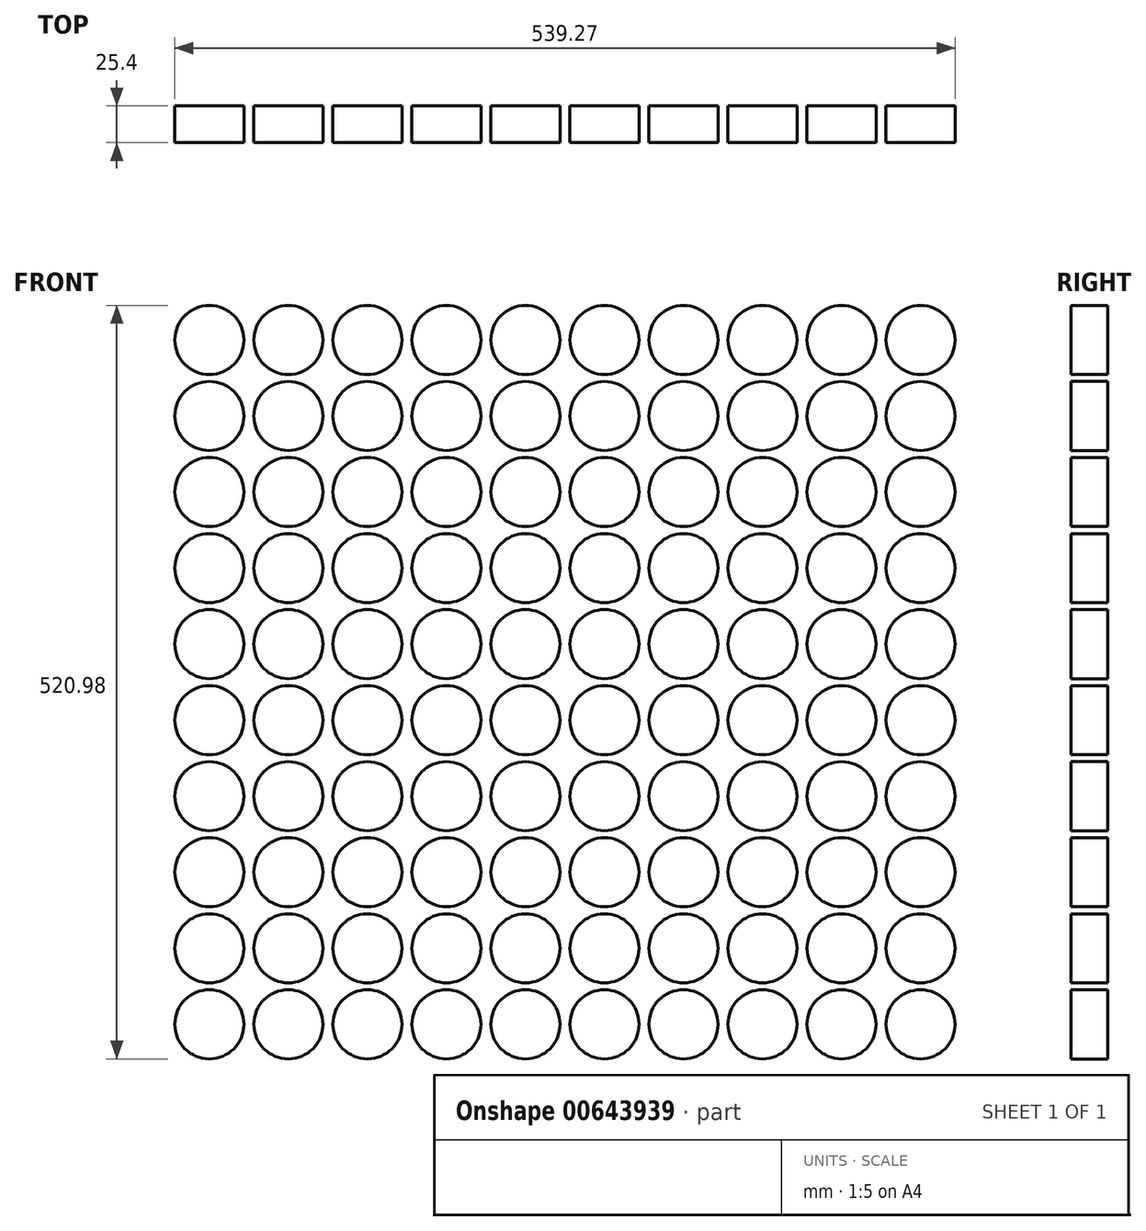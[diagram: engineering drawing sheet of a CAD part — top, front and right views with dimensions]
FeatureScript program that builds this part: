
annotation { "Feature Type Name" : "Feature", "Feature Type Description" : "" }
export const myFeature = defineFeature(function(context is Context, id is Id, definition is map)
    precondition{}
    {
        {
            var Q0;
            Q0=qCreatedBy(makeId("Front.planeOp"),FACE);
            var sketch = newSketch(context, id + "F0", { "sketchPlane" : qUnion([Q0])});
            skCircle(sketch, "E0", {"center": v(-116.75, -34.96) * mm, "radius": 23.89 * mm});
            skCircle(sketch, "E1.0.1.0", {"center": v(-116.75, 17.62) * mm, "radius": 23.89 * mm});
            skCircle(sketch, "E1.0.2.0", {"center": v(-116.75, 70.2) * mm, "radius": 23.89 * mm});
            skCircle(sketch, "E1.0.3.0", {"center": v(-116.75, 122.78) * mm, "radius": 23.89 * mm});
            skCircle(sketch, "E1.0.4.0", {"center": v(-116.75, 175.35) * mm, "radius": 23.89 * mm});
            skCircle(sketch, "E1.0.5.0", {"center": v(-116.75, 227.93) * mm, "radius": 23.89 * mm});
            skCircle(sketch, "E1.0.6.0", {"center": v(-116.75, 280.51) * mm, "radius": 23.89 * mm});
            skCircle(sketch, "E1.0.7.0", {"center": v(-116.75, 333.09) * mm, "radius": 23.89 * mm});
            skCircle(sketch, "E1.0.8.0", {"center": v(-116.75, 385.67) * mm, "radius": 23.89 * mm});
            skCircle(sketch, "E1.0.9.0", {"center": v(-116.75, 438.24) * mm, "radius": 23.89 * mm});
            skCircle(sketch, "E1.1.0.0", {"center": v(-62.14, -34.96) * mm, "radius": 23.89 * mm});
            skCircle(sketch, "E1.1.1.0", {"center": v(-62.14, 17.62) * mm, "radius": 23.89 * mm});
            skCircle(sketch, "E1.1.2.0", {"center": v(-62.14, 70.2) * mm, "radius": 23.89 * mm});
            skCircle(sketch, "E1.1.3.0", {"center": v(-62.14, 122.78) * mm, "radius": 23.89 * mm});
            skCircle(sketch, "E1.1.4.0", {"center": v(-62.14, 175.35) * mm, "radius": 23.89 * mm});
            skCircle(sketch, "E1.1.5.0", {"center": v(-62.14, 227.93) * mm, "radius": 23.89 * mm});
            skCircle(sketch, "E1.1.6.0", {"center": v(-62.14, 280.51) * mm, "radius": 23.89 * mm});
            skCircle(sketch, "E1.1.7.0", {"center": v(-62.14, 333.09) * mm, "radius": 23.89 * mm});
            skCircle(sketch, "E1.1.8.0", {"center": v(-62.14, 385.67) * mm, "radius": 23.89 * mm});
            skCircle(sketch, "E1.1.9.0", {"center": v(-62.14, 438.24) * mm, "radius": 23.89 * mm});
            skCircle(sketch, "E1.2.0.0", {"center": v(-7.53, -34.96) * mm, "radius": 23.89 * mm});
            skCircle(sketch, "E1.2.1.0", {"center": v(-7.53, 17.62) * mm, "radius": 23.89 * mm});
            skCircle(sketch, "E1.2.2.0", {"center": v(-7.53, 70.2) * mm, "radius": 23.89 * mm});
            skCircle(sketch, "E1.2.3.0", {"center": v(-7.53, 122.78) * mm, "radius": 23.89 * mm});
            skCircle(sketch, "E1.2.4.0", {"center": v(-7.53, 175.35) * mm, "radius": 23.89 * mm});
            skCircle(sketch, "E1.2.5.0", {"center": v(-7.53, 227.93) * mm, "radius": 23.89 * mm});
            skCircle(sketch, "E1.2.6.0", {"center": v(-7.53, 280.51) * mm, "radius": 23.89 * mm});
            skCircle(sketch, "E1.2.7.0", {"center": v(-7.53, 333.09) * mm, "radius": 23.89 * mm});
            skCircle(sketch, "E1.2.8.0", {"center": v(-7.53, 385.67) * mm, "radius": 23.89 * mm});
            skCircle(sketch, "E1.2.9.0", {"center": v(-7.53, 438.24) * mm, "radius": 23.89 * mm});
            skCircle(sketch, "E1.3.0.0", {"center": v(47.08, -34.96) * mm, "radius": 23.89 * mm});
            skCircle(sketch, "E1.3.1.0", {"center": v(47.08, 17.62) * mm, "radius": 23.89 * mm});
            skCircle(sketch, "E1.3.2.0", {"center": v(47.08, 70.2) * mm, "radius": 23.89 * mm});
            skCircle(sketch, "E1.3.3.0", {"center": v(47.08, 122.78) * mm, "radius": 23.89 * mm});
            skCircle(sketch, "E1.3.4.0", {"center": v(47.08, 175.35) * mm, "radius": 23.89 * mm});
            skCircle(sketch, "E1.3.5.0", {"center": v(47.08, 227.93) * mm, "radius": 23.89 * mm});
            skCircle(sketch, "E1.3.6.0", {"center": v(47.08, 280.51) * mm, "radius": 23.89 * mm});
            skCircle(sketch, "E1.3.7.0", {"center": v(47.08, 333.09) * mm, "radius": 23.89 * mm});
            skCircle(sketch, "E1.3.8.0", {"center": v(47.08, 385.67) * mm, "radius": 23.89 * mm});
            skCircle(sketch, "E1.3.9.0", {"center": v(47.08, 438.24) * mm, "radius": 23.89 * mm});
            skCircle(sketch, "E1.4.0.0", {"center": v(101.7, -34.96) * mm, "radius": 23.89 * mm});
            skCircle(sketch, "E1.4.1.0", {"center": v(101.7, 17.62) * mm, "radius": 23.89 * mm});
            skCircle(sketch, "E1.4.2.0", {"center": v(101.7, 70.2) * mm, "radius": 23.89 * mm});
            skCircle(sketch, "E1.4.3.0", {"center": v(101.7, 122.78) * mm, "radius": 23.89 * mm});
            skCircle(sketch, "E1.4.4.0", {"center": v(101.7, 175.35) * mm, "radius": 23.89 * mm});
            skCircle(sketch, "E1.4.5.0", {"center": v(101.7, 227.93) * mm, "radius": 23.89 * mm});
            skCircle(sketch, "E1.4.6.0", {"center": v(101.7, 280.51) * mm, "radius": 23.89 * mm});
            skCircle(sketch, "E1.4.7.0", {"center": v(101.7, 333.09) * mm, "radius": 23.89 * mm});
            skCircle(sketch, "E1.4.8.0", {"center": v(101.7, 385.67) * mm, "radius": 23.89 * mm});
            skCircle(sketch, "E1.4.9.0", {"center": v(101.7, 438.24) * mm, "radius": 23.89 * mm});
            skCircle(sketch, "E1.5.0.0", {"center": v(156.3, -34.96) * mm, "radius": 23.89 * mm});
            skCircle(sketch, "E1.5.1.0", {"center": v(156.3, 17.62) * mm, "radius": 23.89 * mm});
            skCircle(sketch, "E1.5.2.0", {"center": v(156.3, 70.2) * mm, "radius": 23.89 * mm});
            skCircle(sketch, "E1.5.3.0", {"center": v(156.3, 122.78) * mm, "radius": 23.89 * mm});
            skCircle(sketch, "E1.5.4.0", {"center": v(156.3, 175.35) * mm, "radius": 23.89 * mm});
            skCircle(sketch, "E1.5.5.0", {"center": v(156.3, 227.93) * mm, "radius": 23.89 * mm});
            skCircle(sketch, "E1.5.6.0", {"center": v(156.3, 280.51) * mm, "radius": 23.89 * mm});
            skCircle(sketch, "E1.5.7.0", {"center": v(156.3, 333.09) * mm, "radius": 23.89 * mm});
            skCircle(sketch, "E1.5.8.0", {"center": v(156.3, 385.67) * mm, "radius": 23.89 * mm});
            skCircle(sketch, "E1.5.9.0", {"center": v(156.3, 438.24) * mm, "radius": 23.89 * mm});
            skCircle(sketch, "E1.6.0.0", {"center": v(210.91, -34.96) * mm, "radius": 23.89 * mm});
            skCircle(sketch, "E1.6.1.0", {"center": v(210.91, 17.62) * mm, "radius": 23.89 * mm});
            skCircle(sketch, "E1.6.2.0", {"center": v(210.91, 70.2) * mm, "radius": 23.89 * mm});
            skCircle(sketch, "E1.6.3.0", {"center": v(210.91, 122.78) * mm, "radius": 23.89 * mm});
            skCircle(sketch, "E1.6.4.0", {"center": v(210.91, 175.35) * mm, "radius": 23.89 * mm});
            skCircle(sketch, "E1.6.5.0", {"center": v(210.91, 227.93) * mm, "radius": 23.89 * mm});
            skCircle(sketch, "E1.6.6.0", {"center": v(210.91, 280.51) * mm, "radius": 23.89 * mm});
            skCircle(sketch, "E1.6.7.0", {"center": v(210.91, 333.09) * mm, "radius": 23.89 * mm});
            skCircle(sketch, "E1.6.8.0", {"center": v(210.91, 385.67) * mm, "radius": 23.89 * mm});
            skCircle(sketch, "E1.6.9.0", {"center": v(210.91, 438.24) * mm, "radius": 23.89 * mm});
            skCircle(sketch, "E1.7.0.0", {"center": v(265.52, -34.96) * mm, "radius": 23.89 * mm});
            skCircle(sketch, "E1.7.1.0", {"center": v(265.52, 17.62) * mm, "radius": 23.89 * mm});
            skCircle(sketch, "E1.7.2.0", {"center": v(265.52, 70.2) * mm, "radius": 23.89 * mm});
            skCircle(sketch, "E1.7.3.0", {"center": v(265.52, 122.78) * mm, "radius": 23.89 * mm});
            skCircle(sketch, "E1.7.4.0", {"center": v(265.52, 175.35) * mm, "radius": 23.89 * mm});
            skCircle(sketch, "E1.7.5.0", {"center": v(265.52, 227.93) * mm, "radius": 23.89 * mm});
            skCircle(sketch, "E1.7.6.0", {"center": v(265.52, 280.51) * mm, "radius": 23.89 * mm});
            skCircle(sketch, "E1.7.7.0", {"center": v(265.52, 333.09) * mm, "radius": 23.89 * mm});
            skCircle(sketch, "E1.7.8.0", {"center": v(265.52, 385.67) * mm, "radius": 23.89 * mm});
            skCircle(sketch, "E1.7.9.0", {"center": v(265.52, 438.24) * mm, "radius": 23.89 * mm});
            skCircle(sketch, "E1.8.0.0", {"center": v(320.13, -34.96) * mm, "radius": 23.89 * mm});
            skCircle(sketch, "E1.8.1.0", {"center": v(320.13, 17.62) * mm, "radius": 23.89 * mm});
            skCircle(sketch, "E1.8.2.0", {"center": v(320.13, 70.2) * mm, "radius": 23.89 * mm});
            skCircle(sketch, "E1.8.3.0", {"center": v(320.13, 122.78) * mm, "radius": 23.89 * mm});
            skCircle(sketch, "E1.8.4.0", {"center": v(320.13, 175.35) * mm, "radius": 23.89 * mm});
            skCircle(sketch, "E1.8.5.0", {"center": v(320.13, 227.93) * mm, "radius": 23.89 * mm});
            skCircle(sketch, "E1.8.6.0", {"center": v(320.13, 280.51) * mm, "radius": 23.89 * mm});
            skCircle(sketch, "E1.8.7.0", {"center": v(320.13, 333.09) * mm, "radius": 23.89 * mm});
            skCircle(sketch, "E1.8.8.0", {"center": v(320.13, 385.67) * mm, "radius": 23.89 * mm});
            skCircle(sketch, "E1.8.9.0", {"center": v(320.13, 438.24) * mm, "radius": 23.89 * mm});
            skCircle(sketch, "E1.9.0.0", {"center": v(374.74, -34.96) * mm, "radius": 23.89 * mm});
            skCircle(sketch, "E1.9.1.0", {"center": v(374.74, 17.62) * mm, "radius": 23.89 * mm});
            skCircle(sketch, "E1.9.2.0", {"center": v(374.74, 70.2) * mm, "radius": 23.89 * mm});
            skCircle(sketch, "E1.9.3.0", {"center": v(374.74, 122.78) * mm, "radius": 23.89 * mm});
            skCircle(sketch, "E1.9.4.0", {"center": v(374.74, 175.35) * mm, "radius": 23.89 * mm});
            skCircle(sketch, "E1.9.5.0", {"center": v(374.74, 227.93) * mm, "radius": 23.89 * mm});
            skCircle(sketch, "E1.9.6.0", {"center": v(374.74, 280.51) * mm, "radius": 23.89 * mm});
            skCircle(sketch, "E1.9.7.0", {"center": v(374.74, 333.09) * mm, "radius": 23.89 * mm});
            skCircle(sketch, "E1.9.8.0", {"center": v(374.74, 385.67) * mm, "radius": 23.89 * mm});
            skCircle(sketch, "E1.9.9.0", {"center": v(374.74, 438.24) * mm, "radius": 23.89 * mm});
            skLineSegment(sketch, "E1.direction1", {"start": v(-116.75, -34.96) * mm, "end": v(-62.14, -34.96) * mm, "construction": true});
            skLineSegment(sketch, "E1.direction2", {"start": v(-116.75, -34.96) * mm, "end": v(-116.75, 17.62) * mm, "construction": true});
            skSolve(sketch);
        }
        {
            var Q0;
            Q0 = qSketchRegion(id + "F0", true);
            extrude(context, id + "F1", {"entities" : qUnion([Q0]), "depth" : 25.4 * mm, "offsetDistance" : 25.4 * mm});
        }
    });
